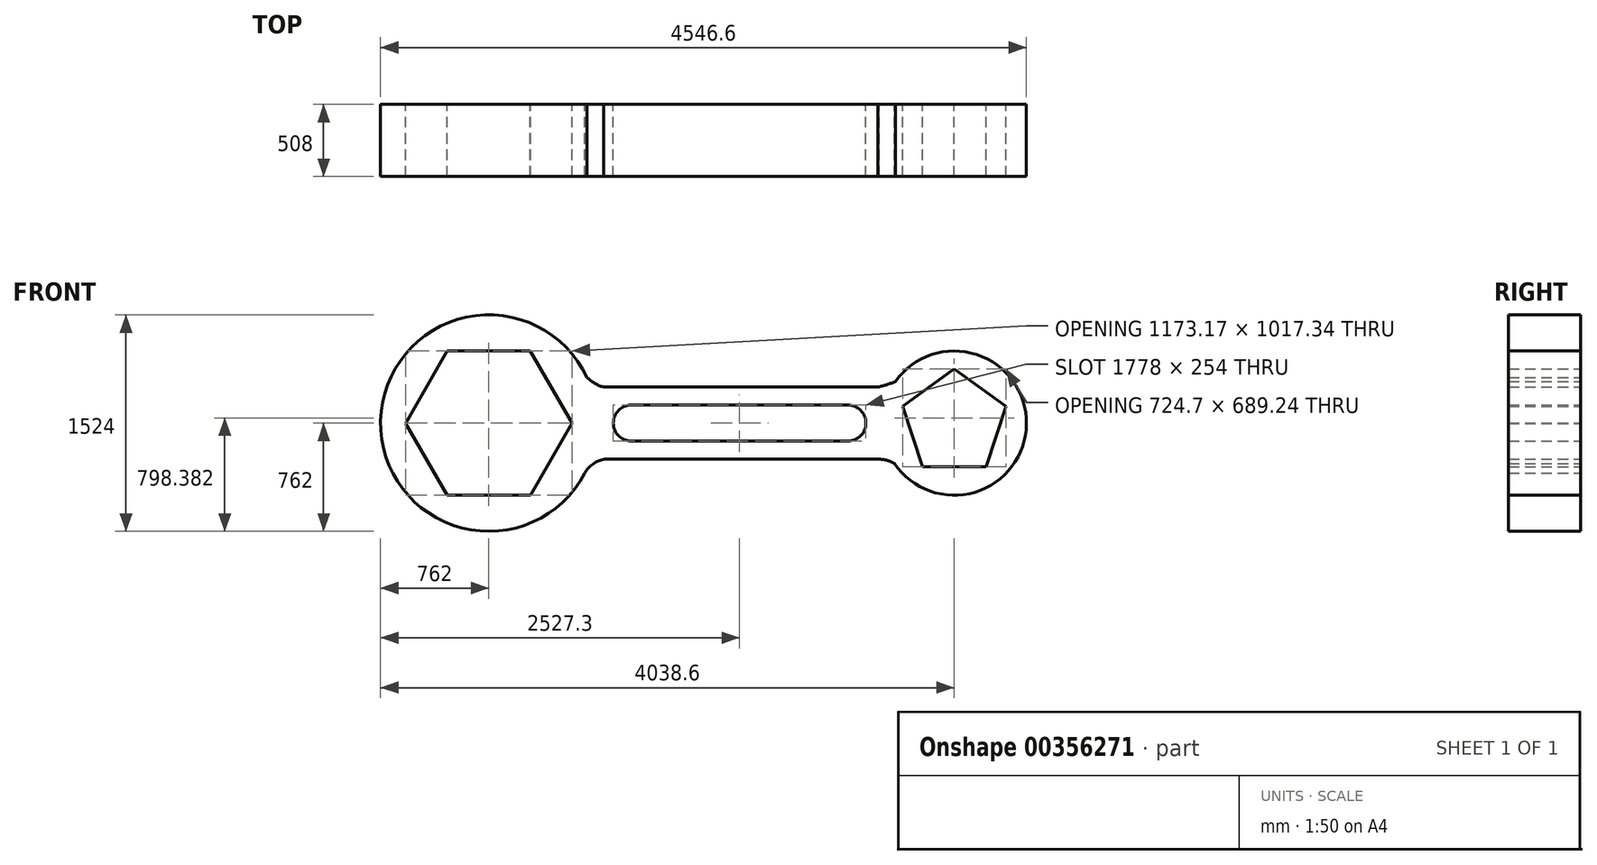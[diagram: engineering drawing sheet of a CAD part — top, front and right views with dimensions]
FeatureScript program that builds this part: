
annotation { "Feature Type Name" : "Feature", "Feature Type Description" : "" }
export const myFeature = defineFeature(function(context is Context, id is Id, definition is map)
    precondition{}
    {
        {
            var Q0;
            Q0=qCreatedBy(makeId("Front.planeOp"),FACE);
            var sketch = newSketch(context, id + "F0", { "sketchPlane" : qUnion([Q0])});
            skCircle(sketch, "E0", {"center": v(0, 0) * mm, "radius": 762 * mm});
            skCircle(sketch, "E1.cCircle", {"center": v(0, 0) * mm, "radius": 508 * mm, "construction": true});
            skLineSegment(sketch, "E1.0", {"start": v(586.59, 1.34) * mm, "end": v(294.45, -507.33) * mm});
            skLineSegment(sketch, "E1.1", {"start": v(294.45, -507.33) * mm, "end": v(-292.13, -508.67) * mm});
            skLineSegment(sketch, "E1.2", {"start": v(-292.13, -508.67) * mm, "end": v(-586.59, -1.34) * mm});
            skLineSegment(sketch, "E1.3", {"start": v(-586.59, -1.34) * mm, "end": v(-294.45, 507.33) * mm});
            skLineSegment(sketch, "E1.4", {"start": v(-294.45, 507.33) * mm, "end": v(292.13, 508.67) * mm});
            skLineSegment(sketch, "E1.5", {"start": v(292.13, 508.67) * mm, "end": v(586.59, 1.34) * mm});
            skPoint(sketch, "E1.0.midPoint", {"position": v(440.52, -253) * mm});
            skCircle(sketch, "E2", {"center": v(3276.6, 0) * mm, "radius": 508 * mm});
            skCircle(sketch, "E3.cCircle", {"center": v(3276.6, 0) * mm, "radius": 308.24 * mm, "construction": true});
            skLineSegment(sketch, "E3.0", {"start": v(3500.55, -308.24) * mm, "end": v(3052.65, -308.24) * mm});
            skLineSegment(sketch, "E3.1", {"start": v(3052.65, -308.24) * mm, "end": v(2914.25, 117.74) * mm});
            skLineSegment(sketch, "E3.2", {"start": v(2914.25, 117.74) * mm, "end": v(3276.6, 381) * mm});
            skLineSegment(sketch, "E3.3", {"start": v(3276.6, 381) * mm, "end": v(3638.95, 117.74) * mm});
            skLineSegment(sketch, "E3.4", {"start": v(3638.95, 117.74) * mm, "end": v(3500.55, -308.24) * mm});
            skPoint(sketch, "E3.0.midPoint", {"position": v(3276.6, -308.24) * mm});
            skLineSegment(sketch, "E4.trimOffspring", {"start": v(806.89, 254) * mm, "end": v(2740.06, 254) * mm});
            skLineSegment(sketch, "E5.trimOffspring", {"start": v(815.96, -254) * mm, "end": v(2749.56, -254) * mm});
            skArc(sketch, "E6", {"start": v(1003.3, 127) * mm, "mid": v(876.3, 0) * mm, "end": v(1003.3, -127) * mm});
            skArc(sketch, "E7", {"start": v(2527.3, -127) * mm, "mid": v(2654.3, 0) * mm, "end": v(2527.3, 127) * mm});
            skLineSegment(sketch, "E8", {"start": v(1003.3, 127) * mm, "end": v(2527.3, 127) * mm});
            skLineSegment(sketch, "E9", {"start": v(1003.3, -127) * mm, "end": v(2527.3, -127) * mm});
            skPoint(sketch, "E10.trimOffspring.end.orphan", {"position": v(2768.6, 0) * mm});
            skPoint(sketch, "E11.orphan", {"position": v(762, 0) * mm});
            skArc(sketch, "E12", {"start": v(690.45, 322.37) * mm, "mid": v(744.31, 280.77) * mm, "end": v(806.89, 254) * mm});
            skArc(sketch, "E13", {"start": v(2740.06, 254) * mm, "mid": v(2802.16, 270.75) * mm, "end": v(2862.2, 293.82) * mm});
            skArc(sketch, "E14", {"start": v(815.96, -254) * mm, "mid": v(734.05, -286.77) * mm, "end": v(675.45, -352.71) * mm});
            skArc(sketch, "E15", {"start": v(2855.41, -284.01) * mm, "mid": v(2804.28, -262.68) * mm, "end": v(2749.56, -254) * mm});
            skSolve(sketch);
        }
        {
            var Q0;
            Q0=makeQuery(id+"F0.imprint","IMPRINT",FACE,{"disambiguationData":[TD([[makeQuery(id+"F0.imprint","IMPRINT",EDGE,{"derivedFrom":sQuery(id+"F0.wireOp",EDGE,"E1.0")}),1.0]])]});
            var Q1;
            {var subQ0=sQuery(id+"F0.wireOp",EDGE,"E4.trimOffspring");Q1=makeQuery(id+"F0.imprint","IMPRINT",FACE,{"disambiguationData":[TD([[makeQuery(id+"F0.imprint","IMPRINT",EDGE,{"derivedFrom":subQ0}),-1.0]])]});}
            var Q2;
            Q2=makeQuery(id+"F0.imprint","IMPRINT",FACE,{"disambiguationData":[TD([[makeQuery(id+"F0.imprint","IMPRINT",EDGE,{"derivedFrom":sQuery(id+"F0.wireOp",EDGE,"E3.0")}),1.0]])]});
            extrude(context, id + "F1", {"entities" : qUnion([Q0, Q1, Q2]), "depth" : 508 * mm});
        }
    });
